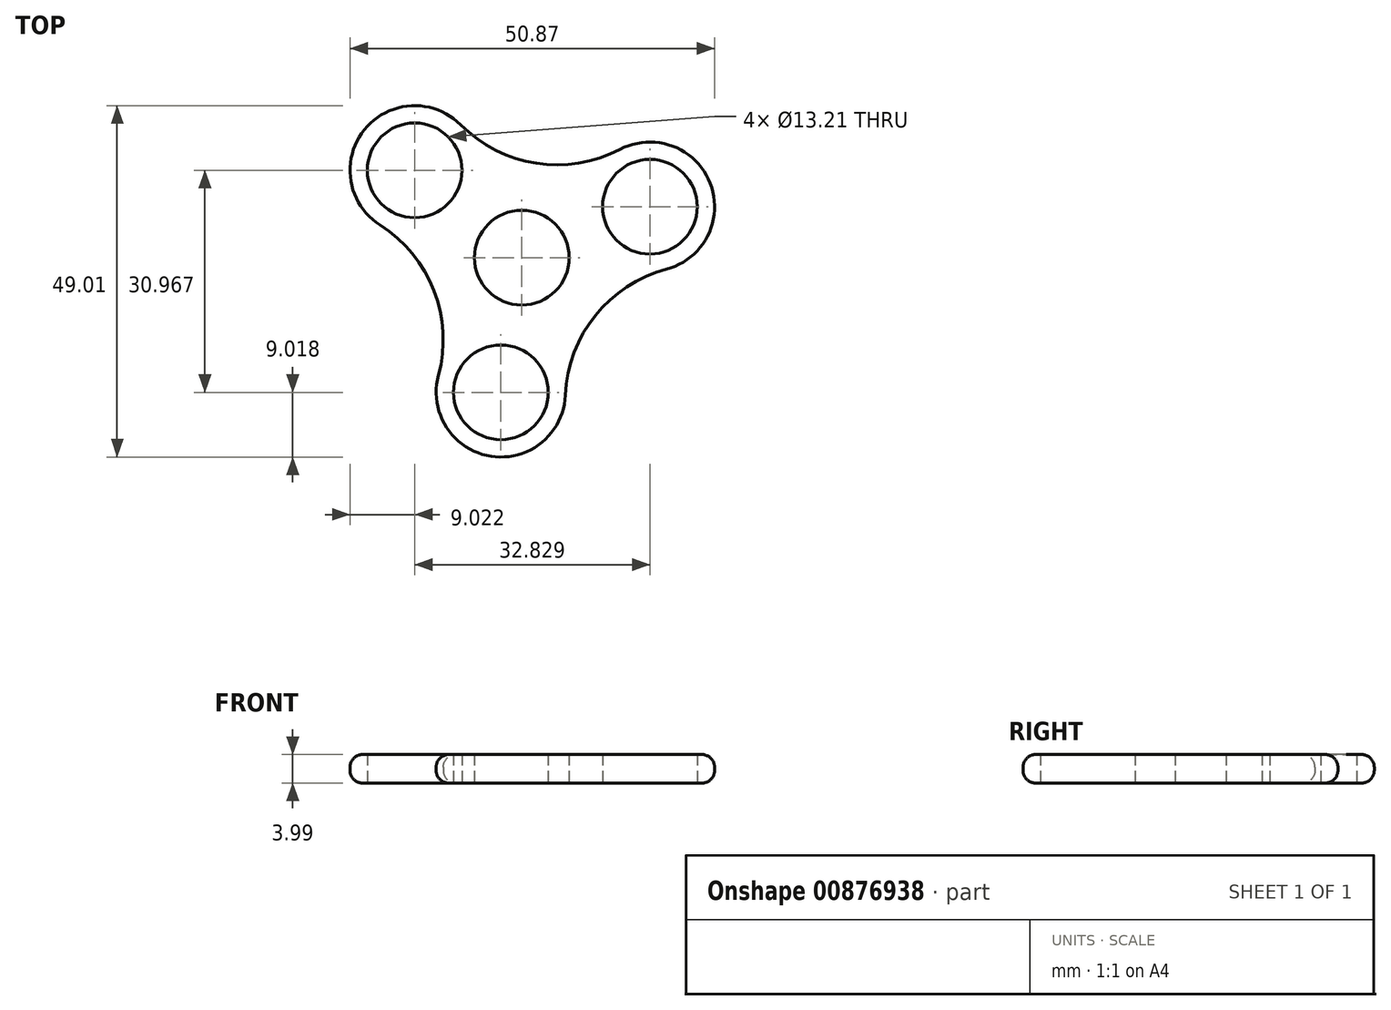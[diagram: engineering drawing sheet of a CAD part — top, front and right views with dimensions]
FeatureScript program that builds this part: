
annotation { "Feature Type Name" : "Feature", "Feature Type Description" : "" }
export const myFeature = defineFeature(function(context is Context, id is Id, definition is map)
    precondition{}
    {
        {
            var Q0;
            Q0=qCreatedBy(makeId("Top.planeOp"),FACE);
            var sketch = newSketch(context, id + "F0", { "sketchPlane" : qUnion([Q0])});
            skCircle(sketch, "E0", {"center": v(-11.58, 4.77) * mm, "radius": 9.02 * mm});
            skCircle(sketch, "E1", {"center": v(9.23, 30.66) * mm, "radius": 9.02 * mm});
            skCircle(sketch, "E2", {"center": v(-23.6, 35.74) * mm, "radius": 9.02 * mm});
            skArc(sketch, "E3", {"start": v(-20.28, 7.13) * mm, "mid": v(-20.9, 18.96) * mm, "end": v(-28.43, 28.12) * mm});
            skArc(sketch, "E4", {"start": v(11.54, 21.94) * mm, "mid": v(1.6, 15.48) * mm, "end": v(-2.56, 4.4) * mm});
            skCircle(sketch, "E5", {"center": v(-23.6, 35.74) * mm, "radius": 6.6 * mm});
            skCircle(sketch, "E6", {"center": v(9.23, 30.66) * mm, "radius": 6.6 * mm});
            skCircle(sketch, "E7", {"center": v(-11.58, 4.77) * mm, "radius": 6.6 * mm});
            skArc(sketch, "E8", {"start": v(-17.2, 42.1) * mm, "mid": v(-6.64, 36.72) * mm, "end": v(5.05, 38.66) * mm});
            skCircle(sketch, "E9", {"center": v(-8.65, 23.55) * mm, "radius": 6.6 * mm});
            skSolve(sketch);
        }
        {
            var Q0;
            Q0=makeQuery(id+"F0.imprint","IMPRINT",FACE,{"disambiguationData":[TD([[makeQuery(id+"F0.imprint","IMPRINT",EDGE,{"derivedFrom":sQuery(id+"F0.wireOp",EDGE,"E5")}),-1.0]])]});
            var Q1;
            Q1=makeQuery(id+"F0.imprint","IMPRINT",FACE,{"disambiguationData":[TD([[makeQuery(id+"F0.imprint","IMPRINT",EDGE,{"derivedFrom":sQuery(id+"F0.wireOp",EDGE,"E6")}),-1.0]])]});
            var Q2;
            {var subQ0=sQuery(id+"F0.wireOp",EDGE,"E3");Q2=makeQuery(id+"F0.imprint","IMPRINT",FACE,{"disambiguationData":[TD([[makeQuery(id+"F0.imprint","IMPRINT",EDGE,{"derivedFrom":subQ0}),-1.0]])]});}
            var Q3;
            Q3=makeQuery(id+"F0.imprint","IMPRINT",FACE,{"disambiguationData":[TD([[makeQuery(id+"F0.imprint","IMPRINT",EDGE,{"derivedFrom":sQuery(id+"F0.wireOp",EDGE,"E7")}),-1.0]])]});
            extrude(context, id + "F1", {"entities" : qUnion([Q0, Q1, Q2, Q3]), "depth" : 4 * mm, "offsetDistance" : 25.4 * mm});
        }
        {
            var Q0;
            Q0=makeQuery(id+"F1.opExtrude","SWEPT_FACE",FACE,{"disambiguationData":[OSD([sQuery(id+"F0.wireOp",EDGE,"E4")])]});
            fillet(context, id + "F2", {"entities" : qUnion([Q0]), "radius" : 1.78 * mm, "tangentPropagation" : true, "allowEdgeOverflow" : false});
        }
    });
